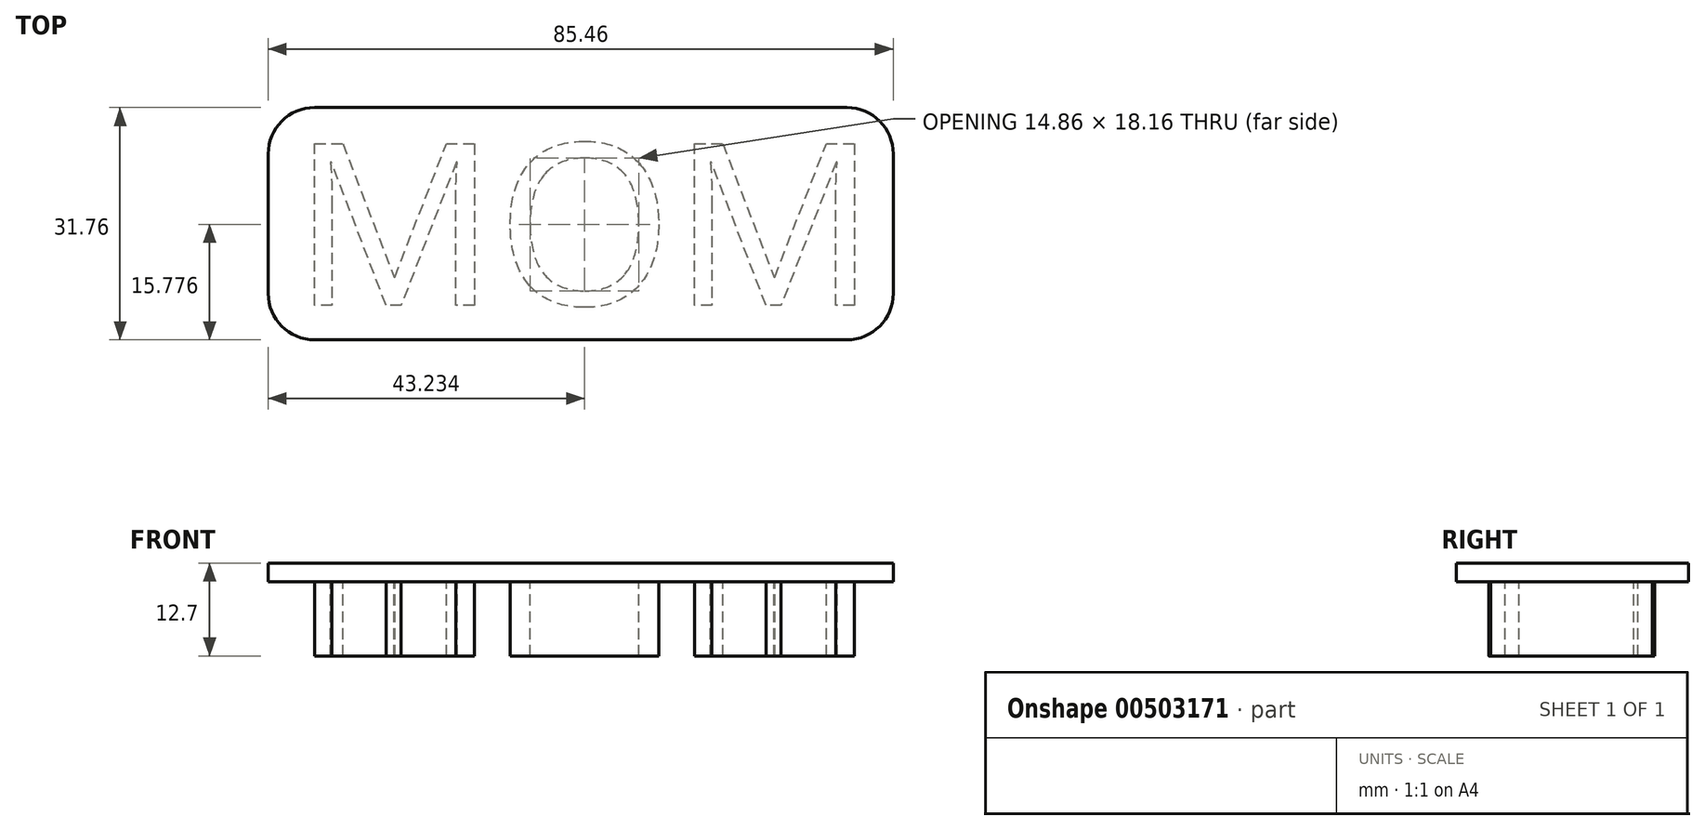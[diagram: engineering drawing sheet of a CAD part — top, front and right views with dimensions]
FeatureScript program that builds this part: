
annotation { "Feature Type Name" : "Feature", "Feature Type Description" : "" }
export const myFeature = defineFeature(function(context is Context, id is Id, definition is map)
    precondition{}
    {
        {
            var Q0;
            Q0=qCreatedBy(makeId("Top.planeOp"),FACE);
            var sketch = newSketch(context, id + "F0", { "sketchPlane" : qUnion([Q0])});
            skText(sketch, "E0", { "text": "MOM", "fontName": "OpenSans-Regular.ttf"});
            const initialGuessF0  = {"E0": [-0.03941, -0.01113, 1, 0, 0.02224]};
            skSetInitialGuess(sketch, initialGuessF0);
            skSolve(sketch);
        }
        {
            var Q0;
            Q0=qSketchRegion(id+"F0",true);
            extrude(context, id + "F1", {"entities" : qUnion([Q0]), "oppositeDirection" : true, "depth" : 10.16 * mm, "offsetDistance" : 25.4 * mm});
        }
        {
            var Q0;
            Q0=qCreatedBy(makeId("Top.planeOp"),FACE);
            var sketch = newSketch(context, id + "F2", { "sketchPlane" : qUnion([Q0])});
            skLineSegment(sketch, "E1.bottom", {"start": v(42.73, -15.87) * mm, "end": v(-42.73, -15.88) * mm});
            skLineSegment(sketch, "E1.top", {"start": v(42.73, 15.88) * mm, "end": v(-42.73, 15.87) * mm});
            skLineSegment(sketch, "E1.left", {"start": v(42.73, 15.88) * mm, "end": v(42.73, -15.87) * mm});
            skLineSegment(sketch, "E1.right", {"start": v(-42.73, -15.88) * mm, "end": v(-42.73, 15.87) * mm});
            skPoint(sketch, "E1.middle", {"position": v(0, 0) * mm});
            skSolve(sketch);
        }
        {
            var Q0;
            Q0=makeQuery(id+"F2.imprint","IMPRINT",FACE,{"disambiguationData":[TD([[makeQuery(id+"F2.imprint","IMPRINT",EDGE,{"derivedFrom":sQuery(id+"F2.wireOp",EDGE,"E1.bottom")}),-1.0]])]});
            extrude(context, id + "F3", {"entities" : qUnion([Q0]), "depth" : 2.54 * mm, "offsetDistance" : 25.4 * mm});
        }
        {
            var Q0;
            Q0=makeQuery(id+"F3.opExtrude","SWEPT_EDGE",EDGE,{"disambiguationData":[OSD([sQuery(id+"F2.wireOp",EDGE,"E1.bottom"),sQuery(id+"F2.wireOp",EDGE,"E1.right")])]});
            var Q1;
            Q1=makeQuery(id+"F3.opExtrude","SWEPT_EDGE",EDGE,{"disambiguationData":[OSD([sQuery(id+"F2.wireOp",EDGE,"E1.top"),sQuery(id+"F2.wireOp",EDGE,"E1.right")])]});
            var Q2;
            Q2=makeQuery(id+"F3.opExtrude","SWEPT_EDGE",EDGE,{"disambiguationData":[OSD([sQuery(id+"F2.wireOp",EDGE,"E1.top"),sQuery(id+"F2.wireOp",EDGE,"E1.left")])]});
            var Q3;
            Q3=makeQuery(id+"F3.opExtrude","SWEPT_EDGE",EDGE,{"disambiguationData":[OSD([sQuery(id+"F2.wireOp",EDGE,"E1.bottom"),sQuery(id+"F2.wireOp",EDGE,"E1.left")])]});
            fillet(context, id + "F4", {"entities" : qUnion([Q0, Q1, Q2, Q3]), "radius" : 6.35 * mm, "tangentPropagation" : true, "allowEdgeOverflow" : false});
        }
    });
